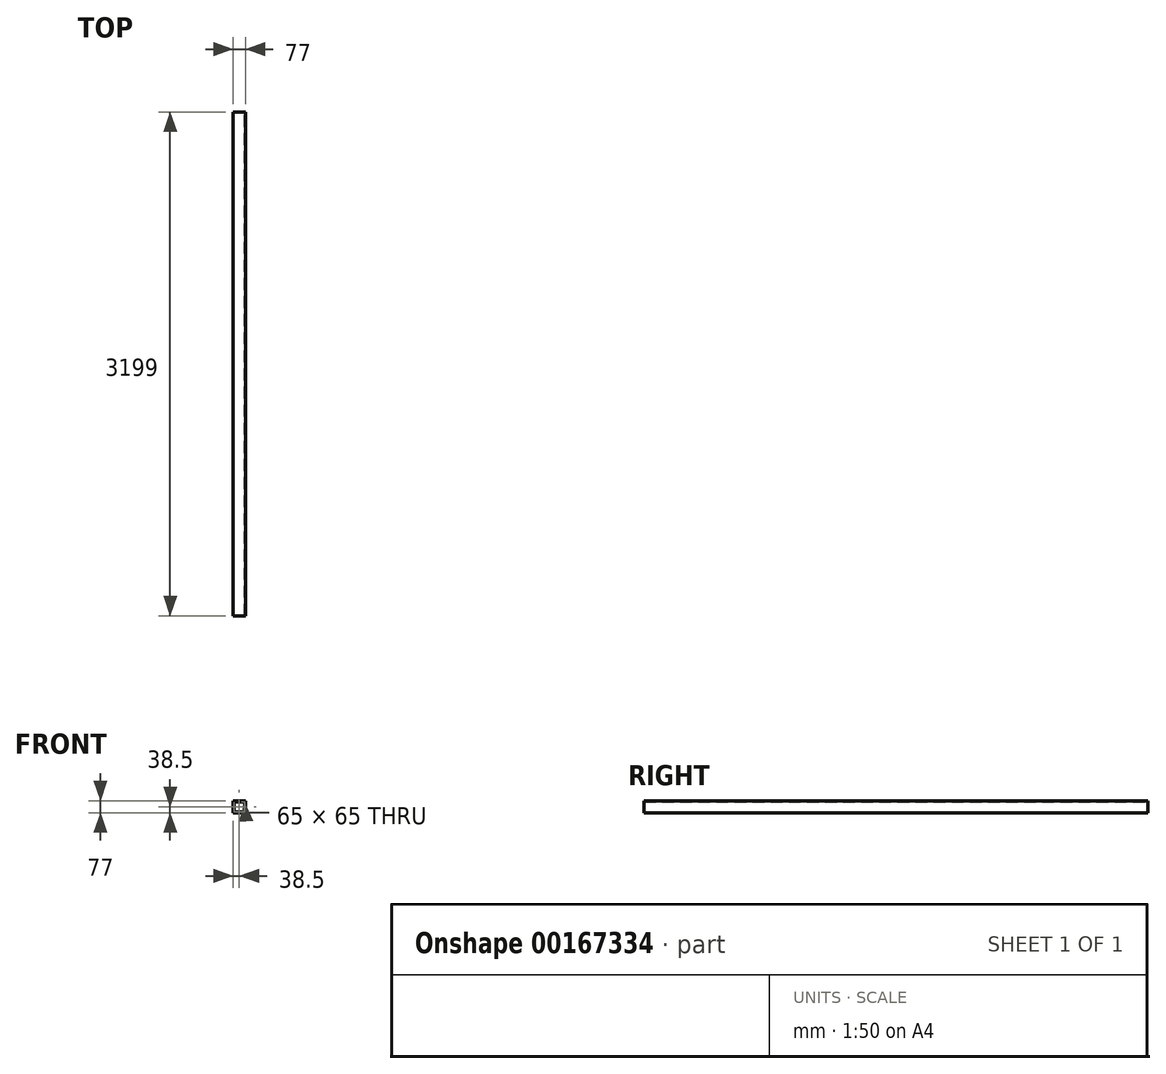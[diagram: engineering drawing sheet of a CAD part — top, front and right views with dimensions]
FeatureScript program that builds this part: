
annotation { "Feature Type Name" : "Feature", "Feature Type Description" : "" }
export const myFeature = defineFeature(function(context is Context, id is Id, definition is map)
    precondition{}
    {
        {
            var Q0;
            Q0=qCreatedBy(makeId("Front.planeOp"),FACE);
            var sketch = newSketch(context, id + "F0", { "sketchPlane" : qUnion([Q0])});
            skLineSegment(sketch, "E0.bottom", {"start": v(0, 0) * mm, "end": v(77, 0) * mm});
            skLineSegment(sketch, "E0.top", {"start": v(0, 77) * mm, "end": v(77, 77) * mm});
            skLineSegment(sketch, "E0.left", {"start": v(0, 0) * mm, "end": v(0, 77) * mm});
            skLineSegment(sketch, "E0.right", {"start": v(77, 0) * mm, "end": v(77, 77) * mm});
            skLineSegment(sketch, "E1.0", {"start": v(6, 6) * mm, "end": v(6, 71) * mm});
            skLineSegment(sketch, "E1.1", {"start": v(6, 6) * mm, "end": v(71, 6) * mm});
            skLineSegment(sketch, "E1.2", {"start": v(71, 6) * mm, "end": v(71, 71) * mm});
            skLineSegment(sketch, "E1.3", {"start": v(6, 71) * mm, "end": v(71, 71) * mm});
            skSolve(sketch);
        }
        {
            var Q0;
            Q0=makeQuery(id+"F0.imprint","IMPRINT",FACE,{"disambiguationData":[TD([[makeQuery(id+"F0.imprint","IMPRINT",EDGE,{"derivedFrom":sQuery(id+"F0.wireOp",EDGE,"E0.bottom")}),1.0]])]});
            extrude(context, id + "F1", {"entities" : qUnion([Q0]), "depth" : 3199 * mm});
        }
    });
